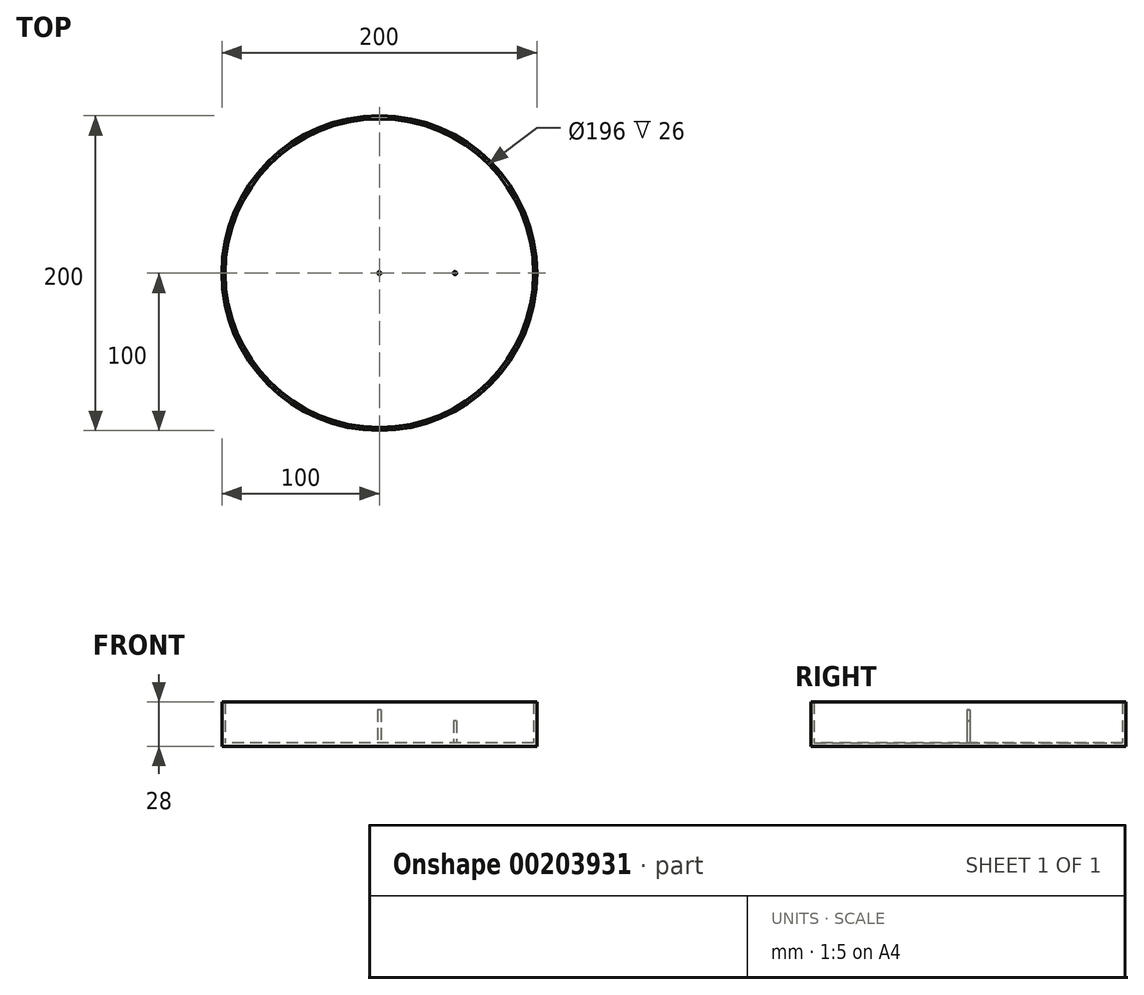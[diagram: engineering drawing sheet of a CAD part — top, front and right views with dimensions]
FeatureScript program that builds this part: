
annotation { "Feature Type Name" : "Feature", "Feature Type Description" : "" }
export const myFeature = defineFeature(function(context is Context, id is Id, definition is map)
    precondition{}
    {
        {
            var Q0;
            Q0=qCreatedBy(makeId("Top.planeOp"),FACE);
            var sketch = newSketch(context, id + "F0", { "sketchPlane" : qUnion([Q0])});
            skCircle(sketch, "E0", {"center": v(0, 0) * mm, "radius": 100 * mm});
            skSolve(sketch);
        }
        {
            var Q0;
            Q0=qSketchRegion(id+"F0",true);
            extrude(context, id + "F1", {"entities" : qUnion([Q0]), "depth" : 28 * mm});
        }
        {
            var Q0;
            Q0=makeQuery(id+"F1.opExtrude","CAP_FACE",FACE,{"disambiguationData":[OSD([sQuery(id+"F0.wireOp",EDGE,"E0")])],"isStart":false});
            shell(context, id + "F2", {"entities" : qUnion([Q0]), "thickness" : 2 * mm});
        }
        {
            var Q0;
            {var subQ0=sQuery(id+"F0.wireOp",EDGE,"E0");Q0=makeQuery(id+"F2.opShell","OFFSET_FACE",FACE,{"disambiguationData":[OSD([subQ0]),TDD([makeQuery(id+"F1.opExtrude","CAP_FACE",FACE,{"disambiguationData":[OSD([subQ0])],"isStart":true})])]});}
            var sketch = newSketch(context, id + "F3", { "sketchPlane" : qUnion([Q0])});
            skCircle(sketch, "E1", {"center": v(0, 0) * mm, "radius": 1 * mm});
            skSolve(sketch);
        }
        {
            var Q0;
            Q0=qSketchRegion(id+"F3",true);
            extrude(context, id + "F4", {"entities" : qUnion([Q0]), "operationType" : NewBodyOperationType.ADD, "depth" : 21 * mm});
        }
        {
            var Q0;
            {var subQ0=sQuery(id+"F0.wireOp",EDGE,"E0");Q0=makeQuery(id+"F2.opShell","OFFSET_FACE",FACE,{"disambiguationData":[OSD([subQ0]),TDD([makeQuery(id+"F1.opExtrude","CAP_FACE",FACE,{"disambiguationData":[OSD([subQ0])],"isStart":true})])]});}
            var sketch = newSketch(context, id + "F5", { "sketchPlane" : qUnion([Q0])});
            skCircle(sketch, "E2", {"center": v(48, 0) * mm, "radius": 1 * mm});
            skSolve(sketch);
        }
        {
            var Q0;
            Q0=qSketchRegion(id+"F5",true);
            extrude(context, id + "F6", {"entities" : qUnion([Q0]), "operationType" : NewBodyOperationType.ADD, "depth" : 14 * mm});
        }
    });
